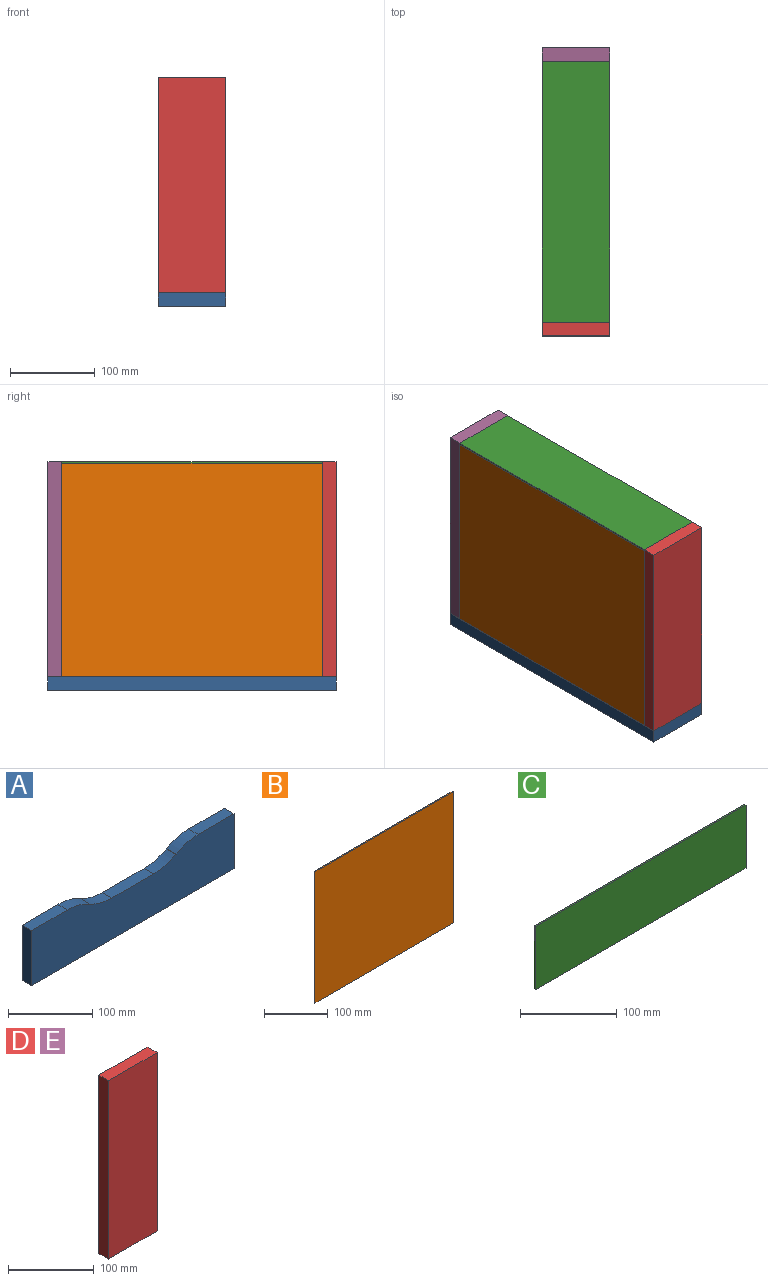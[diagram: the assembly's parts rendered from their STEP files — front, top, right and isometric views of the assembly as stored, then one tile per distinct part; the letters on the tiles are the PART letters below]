
ASSEMBLY  parts=5 mates=12
PART A: 14 faces, bbox 340x16x80 mm
  f0: cylinder r=75mm len=37.21mm, axis (0,1,0), area 623mm2, adj f1,f6,f7,f8
  f1: plane 60.08x16mm, normal (0,0,1), area 961.3mm2, adj f0,f2,f7,f8
  f2: plane 80x16mm, normal (-1,0,0), area 1280mm2, adj f1,f3,f7,f8
  f3: plane 340x16mm, normal (0,0,-1), area 5440mm2, adj f2,f7,f8,f11
  f4: plane 70.17x16mm, normal (0,0,1), area 1122.6mm2, adj f5,f7,f8,f12
  f5: cylinder r=75mm len=37.21mm, axis (0,1,0), area 623mm2, adj f4,f6,f7,f8
  f6: plane 16x0.41mm, normal (0.5,0,0.87), area 7.6mm2, adj f0,f5,f7,f8
  f7: plane 340x80mm, normal (0,-1,0), area 24300mm2, adj f0,f1,f2,f3,f4,f5,f6,f9
  f8: plane 340x80mm, normal (0,1,0), area 24300mm2, adj f0,f1,f2,f3,f4,f5,f6,f9
  f9: cylinder r=75mm len=37.21mm, axis (0,1,0), area 623mm2, adj f7,f8,f10,f13
  f10: plane 60.08x16mm, normal (0,0,1), area 961.3mm2, adj f7,f8,f9,f11
  f11: plane 80x16mm, normal (1,0,0), area 1280mm2, adj f3,f7,f8,f10
  f12: cylinder r=75mm len=37.21mm, axis (0,1,0), area 623mm2, adj f4,f7,f8,f13
  f13: plane 16x0.41mm, normal (-0.5,0,0.87), area 7.6mm2, adj f7,f8,f9,f12
PART B: 6 faces, bbox 308x2x252 mm
  f0: plane 252x2mm, normal (-1,0,0), area 504mm2, adj f1,f3,f4,f5
  f1: plane 308x2mm, normal (0,0,-1), area 616mm2, adj f0,f2,f4,f5
  f2: plane 252x2mm, normal (1,0,0), area 504mm2, adj f1,f3,f4,f5
  f3: plane 308x2mm, normal (0,0,1), area 616mm2, adj f0,f2,f4,f5
  f4: plane 308x252mm, normal (0,-1,0), area 77616mm2, adj f0,f1,f2,f3
  f5: plane 308x252mm, normal (0,1,0), area 77616mm2, adj f0,f1,f2,f3
PART C: 6 faces, bbox 308x2x80 mm
  f0: plane 80x2mm, normal (-1,0,0), area 160mm2, adj f1,f3,f4,f5
  f1: plane 308x2mm, normal (0,0,-1), area 616mm2, adj f0,f2,f4,f5
  f2: plane 80x2mm, normal (1,0,0), area 160mm2, adj f1,f3,f4,f5
  f3: plane 308x2mm, normal (0,0,1), area 616mm2, adj f0,f2,f4,f5
  f4: plane 308x80mm, normal (0,-1,0), area 24640mm2, adj f0,f1,f2,f3
  f5: plane 308x80mm, normal (0,1,0), area 24640mm2, adj f0,f1,f2,f3
PART D: 6 faces, bbox 80x16x254 mm
  f0: plane 80x16mm, normal (0,0,-1), area 1280mm2, adj f1,f3,f4,f5
  f1: plane 254x16mm, normal (1,0,0), area 4064mm2, adj f0,f2,f4,f5
  f2: plane 80x16mm, normal (0,0,1), area 1280mm2, adj f1,f3,f4,f5
  f3: plane 254x16mm, normal (-1,0,0), area 4064mm2, adj f0,f2,f4,f5
  f4: plane 254x80mm, normal (0,-1,0), area 20320mm2, adj f0,f1,f2,f3
  f5: plane 254x80mm, normal (0,1,0), area 20320mm2, adj f0,f1,f2,f3
PART E: same geometry as D
PLACE A rot(axis=(-0.58,0.58,-0.58),120deg) t=(-264.48,-270.82,-1246.88)mm
PLACE B rot(axis=(0,0,-1),90deg) t=(-262.48,106.15,-1230.88)mm
PLACE C rot(axis=(-0.58,0.58,-0.58),120deg) t=(-264.48,545.13,-978.88)mm
PLACE D t=(41.59,-424.82,-1230.88)mm
PLACE E t=(41.59,-100.82,-1230.88)mm
MATE planar A.f11 <-> D.f4  axis (0,-1,0) through (-184.48,-440.82,-1230.88)mm
MATE planar B.f4 <-> E.f3  axis (-1,0,0) through (-264.48,-270.82,-1104.88)mm
MATE planar A.f7 <-> B.f1  axis (0,0,1) through (-194.48,-198.32,-1230.88)mm
MATE planar D.f1 <-> C.f3  axis (1,0,0) through (-184.48,-432.82,-1103.88)mm
MATE planar E.f0 <-> A.f7  axis (0,0,-1) through (-224.48,-108.82,-1230.88)mm
MATE planar C.f2 <-> D.f5  axis (0,-1,0) through (-224.48,-424.82,-977.88)mm
MATE planar D.f1 <-> A.f10  axis (1,0,0) through (-184.48,-432.82,-1230.88)mm
MATE planar C.f4 <-> D.f2  axis (0,0,1) through (-224.48,-270.82,-976.88)mm
MATE planar E.f1 <-> A.f1  axis (1,0,0) through (-184.48,-108.82,-1103.88)mm
MATE planar B.f2 <-> D.f5  axis (0,-1,0) through (-263.48,-424.82,-1104.88)mm
MATE planar A.f7 <-> D.f0  axis (0,0,1) through (-228.2,-270.82,-1230.88)mm
MATE planar A.f2 <-> E.f5  axis (0,1,0) through (-224.48,-100.82,-1238.88)mm
